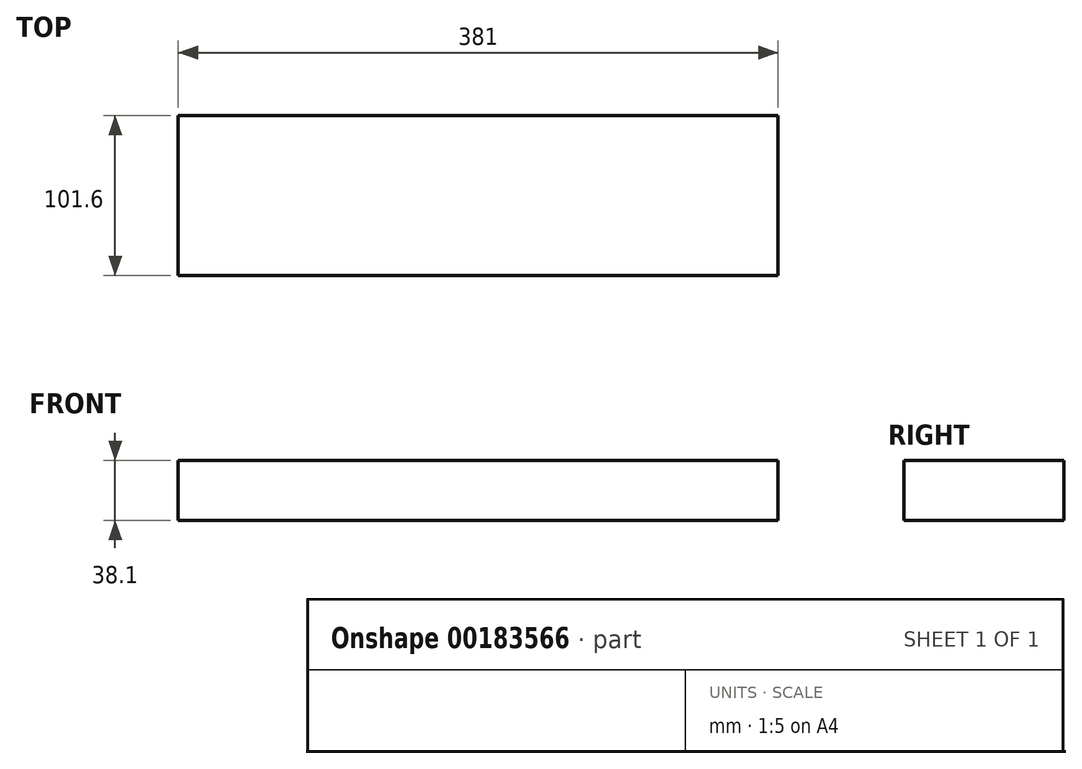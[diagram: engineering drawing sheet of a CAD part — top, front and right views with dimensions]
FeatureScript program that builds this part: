
annotation { "Feature Type Name" : "Feature", "Feature Type Description" : "" }
export const myFeature = defineFeature(function(context is Context, id is Id, definition is map)
    precondition{}
    {
        {
            var Q0;
            Q0=qCreatedBy(makeId("Top.planeOp"),FACE);
            var sketch = newSketch(context, id + "F0", { "sketchPlane" : qUnion([Q0])});
            skLineSegment(sketch, "E0.bottom", {"start": v(0, 0) * mm, "end": v(-381, 0) * mm});
            skLineSegment(sketch, "E0.top", {"start": v(0, 101.6) * mm, "end": v(-381, 101.6) * mm});
            skLineSegment(sketch, "E0.left", {"start": v(0, 0) * mm, "end": v(0, 101.6) * mm});
            skLineSegment(sketch, "E0.right", {"start": v(-381, 0) * mm, "end": v(-381, 101.6) * mm});
            skSolve(sketch);
        }
        {
            var Q0;
            Q0 = qSketchRegion(id + "F0", true);
            extrude(context, id + "F1", {"entities" : qUnion([Q0]), "depth" : 38.1 * mm});
        }
    });
